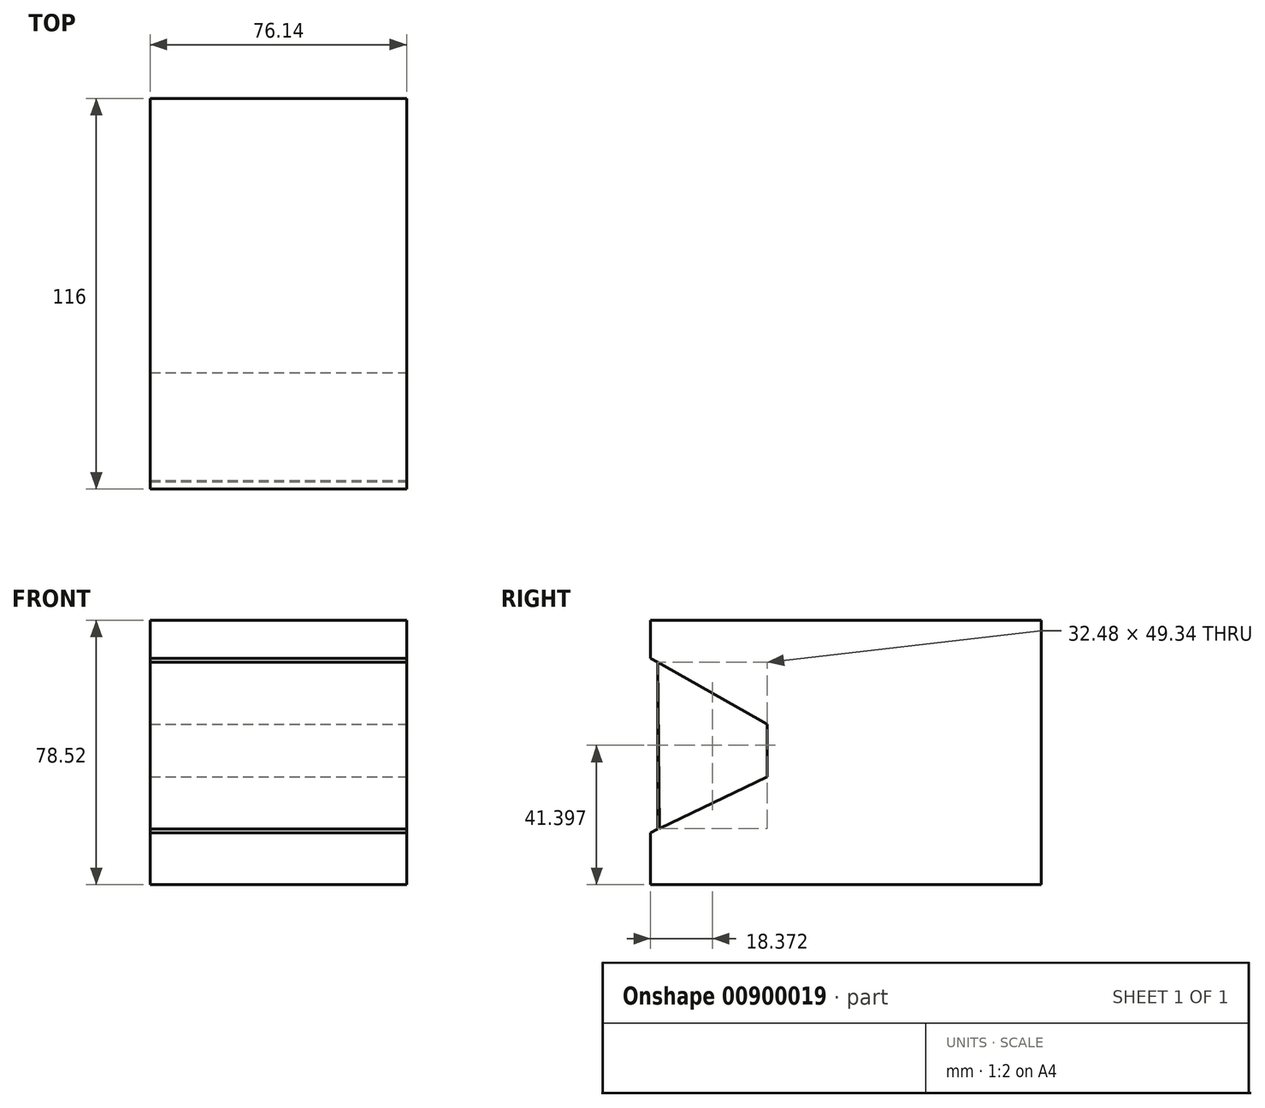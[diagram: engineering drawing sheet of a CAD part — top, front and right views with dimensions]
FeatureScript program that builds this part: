
annotation { "Feature Type Name" : "Feature", "Feature Type Description" : "" }
export const myFeature = defineFeature(function(context is Context, id is Id, definition is map)
    precondition{}
    {
        {
            var Q0;
            Q0=qCreatedBy(makeId("Front.planeOp"),FACE);
            var sketch = newSketch(context, id + "F0", { "sketchPlane" : qUnion([Q0])});
            skLineSegment(sketch, "E0.bottom", {"start": v(38.07, -48.6) * mm, "end": v(-38.07, -48.6) * mm});
            skLineSegment(sketch, "E0.top", {"start": v(38.07, 48.6) * mm, "end": v(-38.07, 48.6) * mm});
            skLineSegment(sketch, "E0.left", {"start": v(38.07, -48.6) * mm, "end": v(38.07, 48.6) * mm});
            skLineSegment(sketch, "E0.right", {"start": v(-38.07, -48.6) * mm, "end": v(-38.07, 48.6) * mm});
            skPoint(sketch, "E0.middle", {"position": v(0, 0) * mm});
            skSolve(sketch);
        }
        {
            var Q0;
            Q0 = qSketchRegion(id + "F0", true);
            extrude(context, id + "F1", {"entities" : qUnion([Q0]), "endBound" : BoundingType.SYMMETRIC, "depth" : 116 * mm, "offsetDistance" : 25 * mm});
        }
        {
            var Q0;
            Q0=makeQuery(id+"F1.opExtrude","SWEPT_FACE",FACE,{"disambiguationData":[OSD([sQuery(id+"F0.wireOp",EDGE,"E0.top")])]});
            var sketch = newSketch(context, id + "F2", { "sketchPlane" : qUnion([Q0])});
            skSolve(sketch);
        }
        {
            var Q0;
            Q0 = qSketchRegion(id + "F2", true);
            var Q1;
            {var subQ0=sQuery(id+"F0.wireOp",EDGE,"E0.top");Q1=makeQuery(id+"F2.imprint","IMPRINT",FACE,{"disambiguationData":[TD([[makeQuery(id+"F2.imprint","IMPRINT",EDGE,{"derivedFrom":makeQuery(id+"F1.opExtrude","CAP_EDGE",EDGE,{"disambiguationData":[OSD([subQ0])],"isStart":true})}),1.0]])]});}
            extrude(context, id + "F3", {"entities" : qUnion([Q0, Q1]), "operationType" : NewBodyOperationType.REMOVE, "oppositeDirection" : true, "depth" : 18.7 * mm, "offsetDistance" : 25 * mm});
        }
        {
            var Q0;
            Q0=qCreatedBy(makeId("Right.planeOp"),FACE);
            var sketch = newSketch(context, id + "F4", { "sketchPlane" : qUnion([Q0])});
            skLineSegment(sketch, "E1", {"start": v(-55.87, 17.46) * mm, "end": v(-55.4, -31.88) * mm});
            skLineSegment(sketch, "E2", {"start": v(-55.4, -31.88) * mm, "end": v(-23.39, -16.52) * mm});
            skLineSegment(sketch, "E3", {"start": v(-23.39, -16.52) * mm, "end": v(-23.39, -1) * mm});
            skLineSegment(sketch, "E4", {"start": v(-23.39, -1) * mm, "end": v(-55.87, 17.46) * mm});
            skSolve(sketch);
        }
        {
            var Q0;
            Q0 = qSketchRegion(id + "F4", true);
            extrude(context, id + "F5", {"entities" : qUnion([Q0]), "operationType" : NewBodyOperationType.REMOVE, "endBound" : BoundingType.SYMMETRIC, "oppositeDirection" : true, "depth" : 246.2 * mm, "offsetDistance" : 25 * mm});
        }
        {
            var Q0;
            Q0=qCreatedBy(makeId("Right.planeOp"),FACE);
            var sketch = newSketch(context, id + "F6", { "sketchPlane" : qUnion([Q0])});
            skLineSegment(sketch, "E5.left", {"start": v(-55.87, 17.46) * mm, "end": v(-55.87, 17.3) * mm});
            skLineSegment(sketch, "E5.right", {"start": v(-58, 17.46) * mm, "end": v(-58, 17.3) * mm});
            skLineSegment(sketch, "E6", {"start": v(-48.88, -28.74) * mm, "end": v(-58.06, -33.16) * mm});
            skLineSegment(sketch, "E7", {"start": v(-48.5, 13.28) * mm, "end": v(-58, 18.67) * mm});
            skLineSegment(sketch, "E8", {"start": v(-58, 18.67) * mm, "end": v(-58.06, -33.16) * mm});
            skLineSegment(sketch, "E9", {"start": v(-55.87, 17.3) * mm, "end": v(-55.87, -32.1) * mm});
            skLineSegment(sketch, "E10", {"start": v(-55.87, -32.1) * mm, "end": v(-58.06, -33.16) * mm});
            skSolve(sketch);
        }
        {
            var Q0;
            Q0 = qSketchRegion(id + "F6", true);
            extrude(context, id + "F7", {"entities" : qUnion([Q0]), "operationType" : NewBodyOperationType.REMOVE, "endBound" : BoundingType.SYMMETRIC, "oppositeDirection" : true, "depth" : 179 * mm, "offsetDistance" : 25 * mm});
        }
    });
